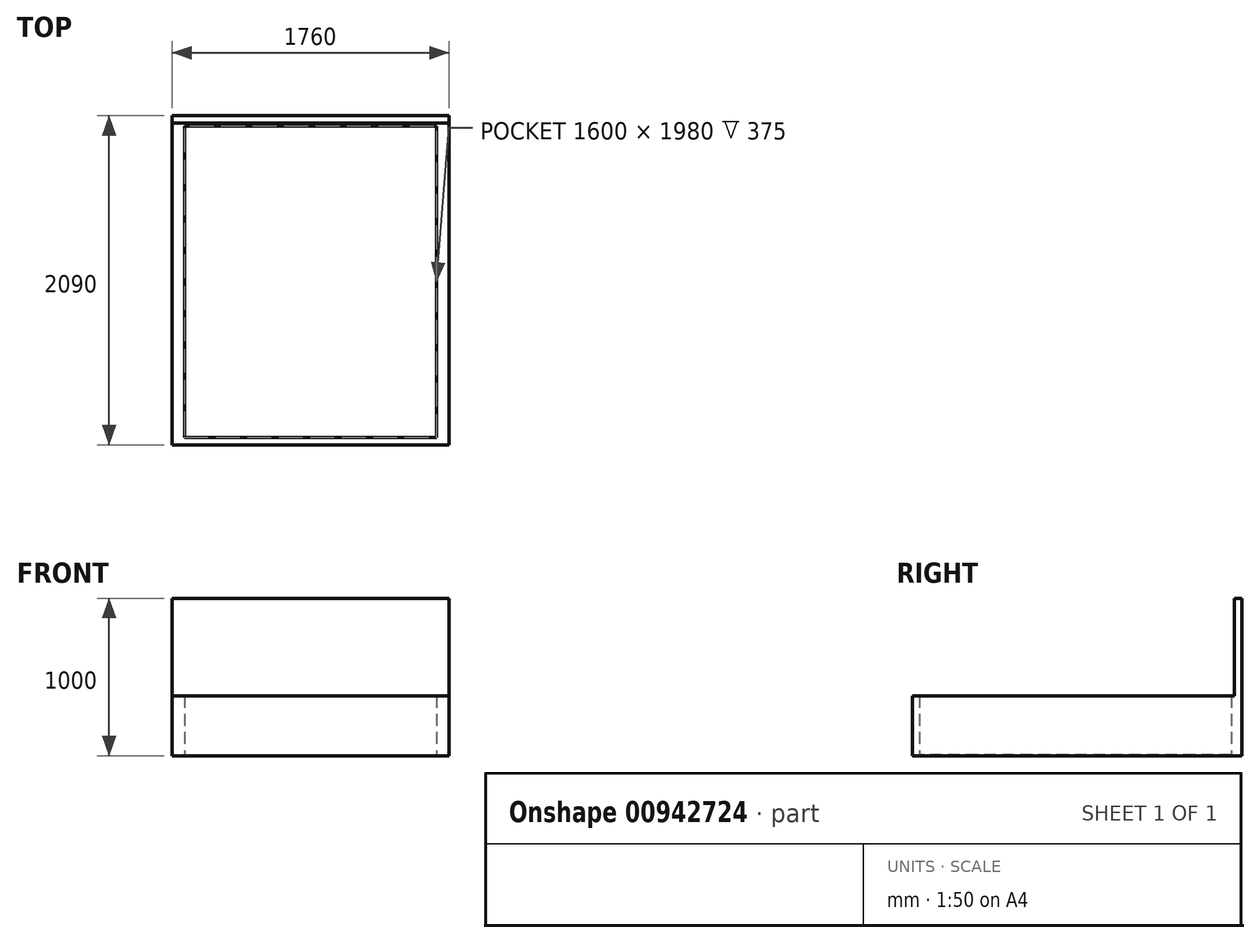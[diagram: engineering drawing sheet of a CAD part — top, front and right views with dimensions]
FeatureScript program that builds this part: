
annotation { "Feature Type Name" : "Feature", "Feature Type Description" : "" }
export const myFeature = defineFeature(function(context is Context, id is Id, definition is map)
    precondition{}
    {
        {
            var Q0;
            Q0=qCreatedBy(makeId("Top.planeOp"),FACE);
            var sketch = newSketch(context, id + "F0", { "sketchPlane" : qUnion([Q0])});
            skLineSegment(sketch, "E0.bottom", {"start": v(-880, 1045) * mm, "end": v(880, 1045) * mm});
            skLineSegment(sketch, "E0.top", {"start": v(-880, -1045) * mm, "end": v(880, -1045) * mm});
            skLineSegment(sketch, "E0.left", {"start": v(-880, 1045) * mm, "end": v(-880, -1045) * mm});
            skLineSegment(sketch, "E0.right", {"start": v(880, 1045) * mm, "end": v(880, -1045) * mm});
            skLineSegment(sketch, "E1", {"start": v(-880, 0) * mm, "end": v(0, 0) * mm, "construction": true});
            skLineSegment(sketch, "E2", {"start": v(0, 0) * mm, "end": v(880, 0) * mm, "construction": true});
            skLineSegment(sketch, "E3", {"start": v(0, -1045) * mm, "end": v(0, 0) * mm, "construction": true});
            skLineSegment(sketch, "E4", {"start": v(0, 0) * mm, "end": v(0, 1045) * mm, "construction": true});
            skLineSegment(sketch, "E5.bottom", {"start": v(-800, 1000) * mm, "end": v(800, 1000) * mm});
            skLineSegment(sketch, "E5.top", {"start": v(-800, -1000) * mm, "end": v(800, -1000) * mm});
            skLineSegment(sketch, "E5.left", {"start": v(-800, 980) * mm, "end": v(-800, -1000) * mm});
            skLineSegment(sketch, "E5.right", {"start": v(800, 980) * mm, "end": v(800, -1000) * mm});
            skLineSegment(sketch, "E6", {"start": v(-800, 1000) * mm, "end": v(-880, 1000) * mm});
            skLineSegment(sketch, "E7", {"start": v(800, 1000) * mm, "end": v(880, 1000) * mm});
            skLineSegment(sketch, "E8", {"start": v(-800, 980) * mm, "end": v(800, 980) * mm});
            skSolve(sketch);
        }
        {
            var Q0;
            {var subQ1=sQuery(id+"F0.wireOp",EDGE,"E0.top");Q0=makeQuery(id+"F0.imprint","IMPRINT",FACE,{"disambiguationData":[TD([[makeQuery(id+"F0.imprint","IMPRINT",EDGE,{"derivedFrom":subQ1}),1.0]])]});}
            extrude(context, id + "F1", {"entities" : qUnion([Q0]), "depth" : 380 * mm, "offsetDistance" : 25 * mm});
        }
        {
            var Q0;
            {var subQ1=sQuery(id+"F0.wireOp",EDGE,"E0.bottom");Q0=makeQuery(id+"F0.imprint","IMPRINT",FACE,{"disambiguationData":[TD([[makeQuery(id+"F0.imprint","IMPRINT",EDGE,{"derivedFrom":subQ1}),-1.0]])]});}
            extrude(context, id + "F2", {"entities" : qUnion([Q0]), "operationType" : NewBodyOperationType.ADD, "depth" : 1000 * mm, "offsetDistance" : 25 * mm});
        }
        {
            var Q0;
            Q0=makeQuery(id+"F0.imprint","IMPRINT",FACE,{"disambiguationData":[TD([[makeQuery(id+"F0.imprint","IMPRINT",EDGE,{"derivedFrom":sQuery(id+"F0.wireOp",EDGE,"E5.top")}),1.0]])]});
            extrude(context, id + "F3", {"entities" : qUnion([Q0]), "operationType" : NewBodyOperationType.ADD, "depth" : 5 * mm, "offsetDistance" : 25 * mm});
        }
    });
